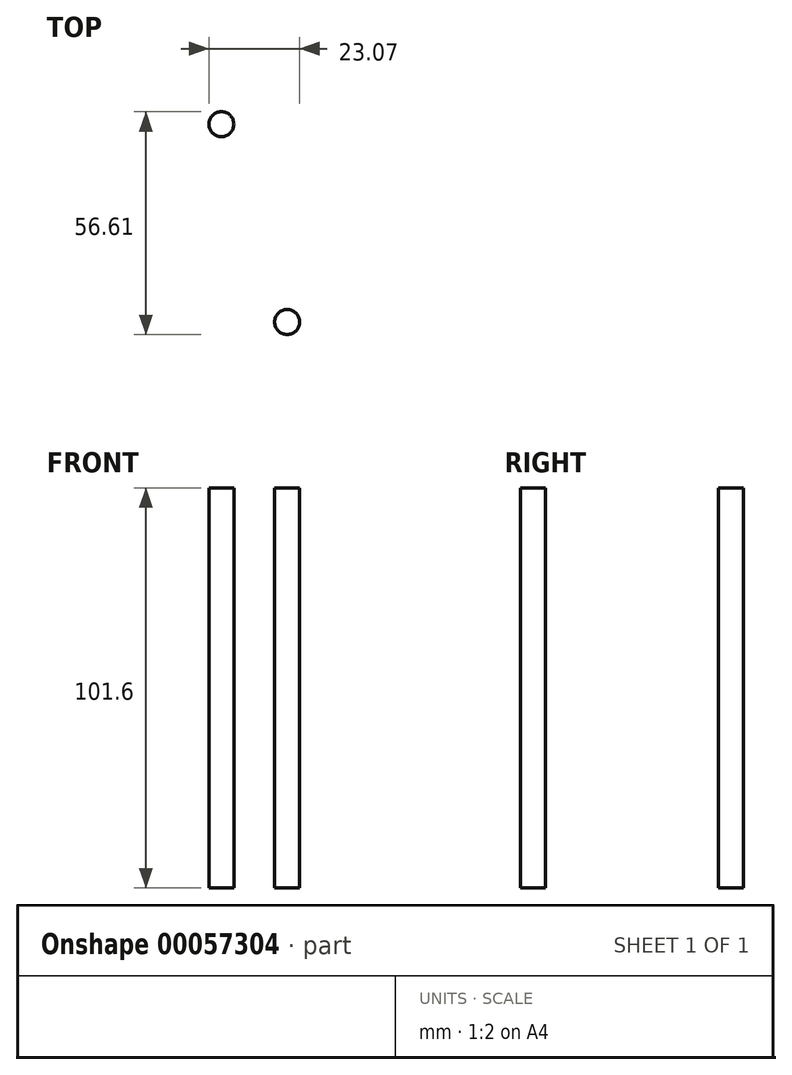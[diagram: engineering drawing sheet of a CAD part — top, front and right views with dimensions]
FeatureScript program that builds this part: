
annotation { "Feature Type Name" : "Feature", "Feature Type Description" : "" }
export const myFeature = defineFeature(function(context is Context, id is Id, definition is map)
    precondition{}
    {
        {
            var Q0;
            Q0=qCreatedBy(makeId("Top.planeOp"),FACE);
            var sketch = newSketch(context, id + "F0", { "sketchPlane" : qUnion([Q0])});
            skCircle(sketch, "E0", {"center": v(-49.9, 37.81) * mm, "radius": 3.18 * mm});
            skCircle(sketch, "E1", {"center": v(-33.17, -12.45) * mm, "radius": 3.18 * mm});
            skSolve(sketch);
        }
        {
            var Q0;
            Q0 = qSketchRegion(id + "F0", true);
            extrude(context, id + "F1", {"entities" : qUnion([Q0]), "depth" : 101.6 * mm});
        }
    });
